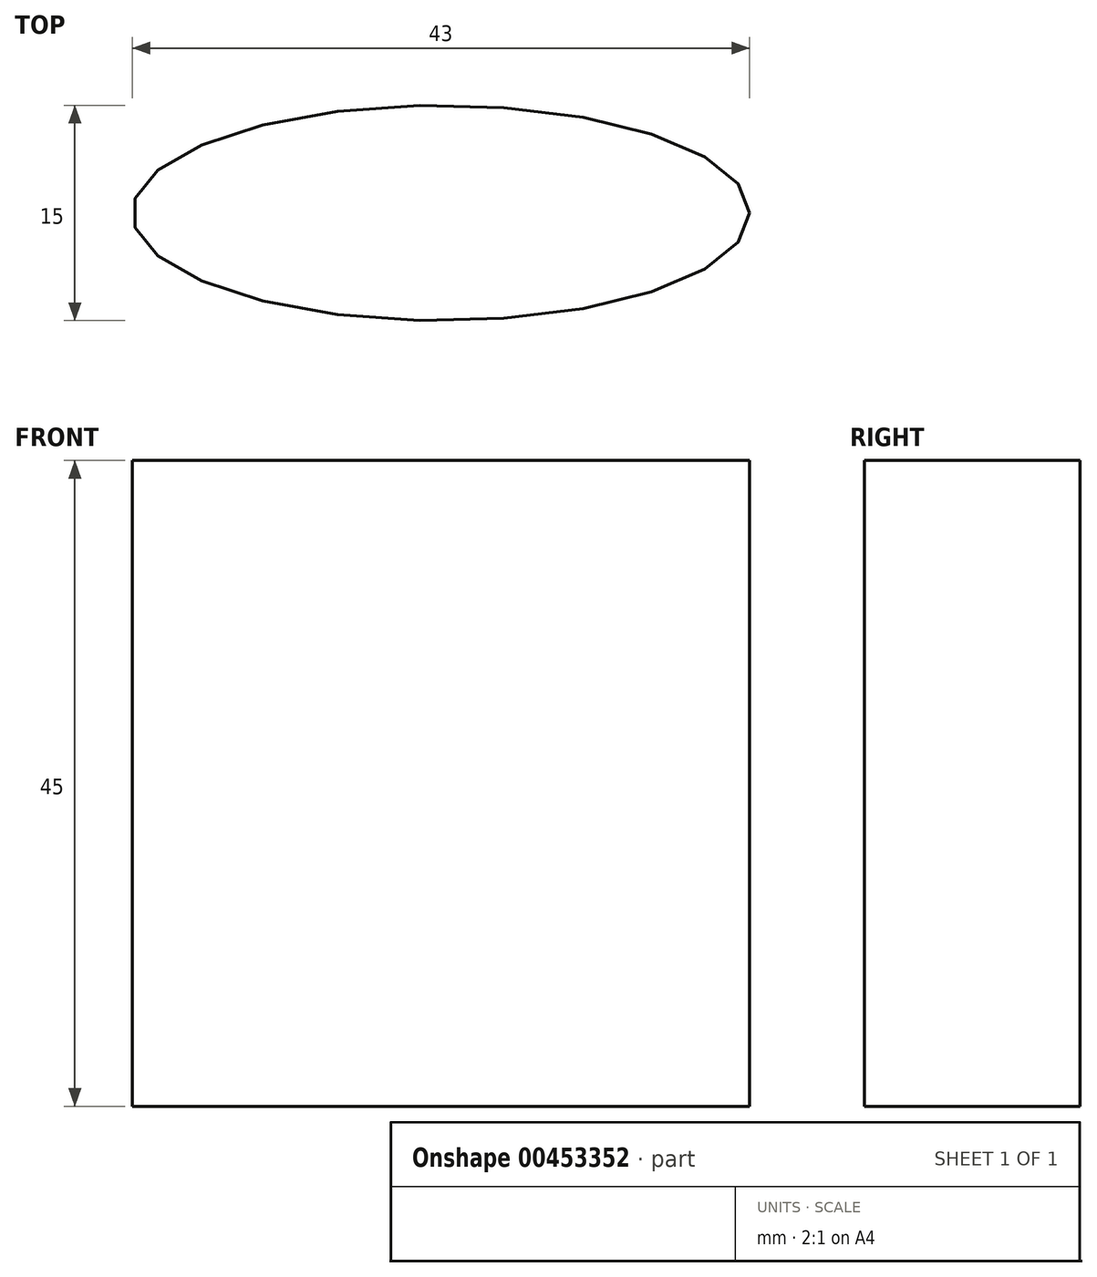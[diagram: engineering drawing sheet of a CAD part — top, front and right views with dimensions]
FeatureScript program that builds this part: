
annotation { "Feature Type Name" : "Feature", "Feature Type Description" : "" }
export const myFeature = defineFeature(function(context is Context, id is Id, definition is map)
    precondition{}
    {
        {
            var Q0;
            Q0=qCreatedBy(makeId("Top.planeOp"),FACE);
            var sketch = newSketch(context, id + "F0", { "sketchPlane" : qUnion([Q0])});
            skEllipse(sketch, "E0", {"center": v(0, 0) * mm, "majorRadius": 21.5 * mm, "minorRadius": 7.5 * mm, "majorAxis": v(1, 0)});
            skFitSpline(sketch, "E1.0", {"points": [v(19.88, -0.29) * mm, v(19.91, 0) * mm, v(19.88, 0.29) * mm, v(19.73, 0.66) * mm, v(19.4, 1.12) * mm, v(18.87, 1.64) * mm, v(18.12, 2.2) * mm, v(16.84, 2.94) * mm, v(14.78, 3.82) * mm, v(12.2, 4.56) * mm, v(9.85, 5.05) * mm, v(7.4, 5.46) * mm, v(4.77, 5.74) * mm, v(2.06, 5.88) * mm, v(0, 5.91) * mm, v(-2.06, 5.88) * mm, v(-4.77, 5.74) * mm, v(-7.4, 5.46) * mm, v(-9.85, 5.05) * mm, v(-12.2, 4.56) * mm, v(-14.78, 3.82) * mm, v(-16.84, 2.94) * mm, v(-18.12, 2.2) * mm, v(-18.87, 1.64) * mm, v(-19.4, 1.12) * mm, v(-19.73, 0.66) * mm, v(-19.88, 0.29) * mm, v(-19.91, 0) * mm, v(-19.88, -0.29) * mm, v(-19.73, -0.66) * mm, v(-19.4, -1.12) * mm, v(-18.87, -1.64) * mm, v(-18.12, -2.2) * mm, v(-16.84, -2.94) * mm, v(-14.78, -3.82) * mm, v(-12.2, -4.56) * mm, v(-9.85, -5.05) * mm, v(-7.4, -5.46) * mm, v(-4.77, -5.74) * mm, v(-2.06, -5.88) * mm, v(0, -5.91) * mm, v(2.06, -5.88) * mm, v(4.77, -5.74) * mm, v(7.4, -5.46) * mm, v(9.85, -5.05) * mm, v(12.2, -4.56) * mm, v(14.78, -3.82) * mm, v(16.84, -2.94) * mm, v(18.12, -2.2) * mm, v(18.87, -1.64) * mm, v(19.4, -1.12) * mm, v(19.73, -0.66) * mm, v(19.88, -0.29) * mm, v(19.91, 0) * mm, v(19.88, 0.29) * mm, v(19.88, -0.29) * mm]});
            skFitSpline(sketch, "E2.0", {"points": [v(24.46, -0.8) * mm, v(24.52, 0) * mm, v(24.46, 0.8) * mm, v(24.24, 1.82) * mm, v(23.73, 2.99) * mm, v(22.87, 4.17) * mm, v(21.82, 5.18) * mm, v(20.63, 6.06) * mm, v(18.83, 7.1) * mm, v(16.27, 8.18) * mm, v(13.3, 9.03) * mm, v(10.7, 9.58) * mm, v(7.98, 10.02) * mm, v(5.14, 10.32) * mm, v(2.22, 10.47) * mm, v(0, 10.51) * mm, v(-2.22, 10.47) * mm, v(-5.14, 10.32) * mm, v(-7.98, 10.02) * mm, v(-10.7, 9.58) * mm, v(-13.3, 9.03) * mm, v(-16.27, 8.18) * mm, v(-18.83, 7.1) * mm, v(-20.63, 6.06) * mm, v(-21.82, 5.18) * mm, v(-22.87, 4.17) * mm, v(-23.73, 2.99) * mm, v(-24.24, 1.82) * mm, v(-24.46, 0.8) * mm, v(-24.52, 0) * mm, v(-24.46, -0.8) * mm, v(-24.24, -1.82) * mm, v(-23.73, -2.99) * mm, v(-22.87, -4.17) * mm, v(-21.82, -5.18) * mm, v(-20.63, -6.06) * mm, v(-18.83, -7.1) * mm, v(-16.27, -8.18) * mm, v(-13.3, -9.03) * mm, v(-10.7, -9.58) * mm, v(-7.98, -10.02) * mm, v(-5.14, -10.32) * mm, v(-2.22, -10.47) * mm, v(0, -10.51) * mm, v(2.22, -10.47) * mm, v(5.14, -10.32) * mm, v(7.98, -10.02) * mm, v(10.7, -9.58) * mm, v(13.3, -9.03) * mm, v(16.27, -8.18) * mm, v(18.83, -7.1) * mm, v(20.63, -6.06) * mm, v(21.82, -5.18) * mm, v(22.87, -4.17) * mm, v(23.73, -2.99) * mm, v(24.24, -1.82) * mm, v(24.46, -0.8) * mm, v(24.52, 0) * mm, v(24.46, 0.8) * mm, v(24.46, -0.8) * mm]});
            skSolve(sketch);
        }
        {
            var Q0;
            Q0 = qSketchRegion(id + "F0", true);
            extrude(context, id + "F1", {"entities" : qUnion([Q0]), "depth" : 1 * mm});
        }
        {
            var Q0;
            Q0=makeQuery(id+"F0.imprint","IMPRINT",FACE,{"disambiguationData":[TD([[makeQuery(id+"F0.imprint","IMPRINT",EDGE,{"derivedFrom":sQuery(id+"F0.wireOp",EDGE,"E0")}),1.0]])]});
            extrude(context, id + "F2", {"entities" : qUnion([Q0]), "operationType" : NewBodyOperationType.ADD, "depth" : 45 * mm});
        }
    });
